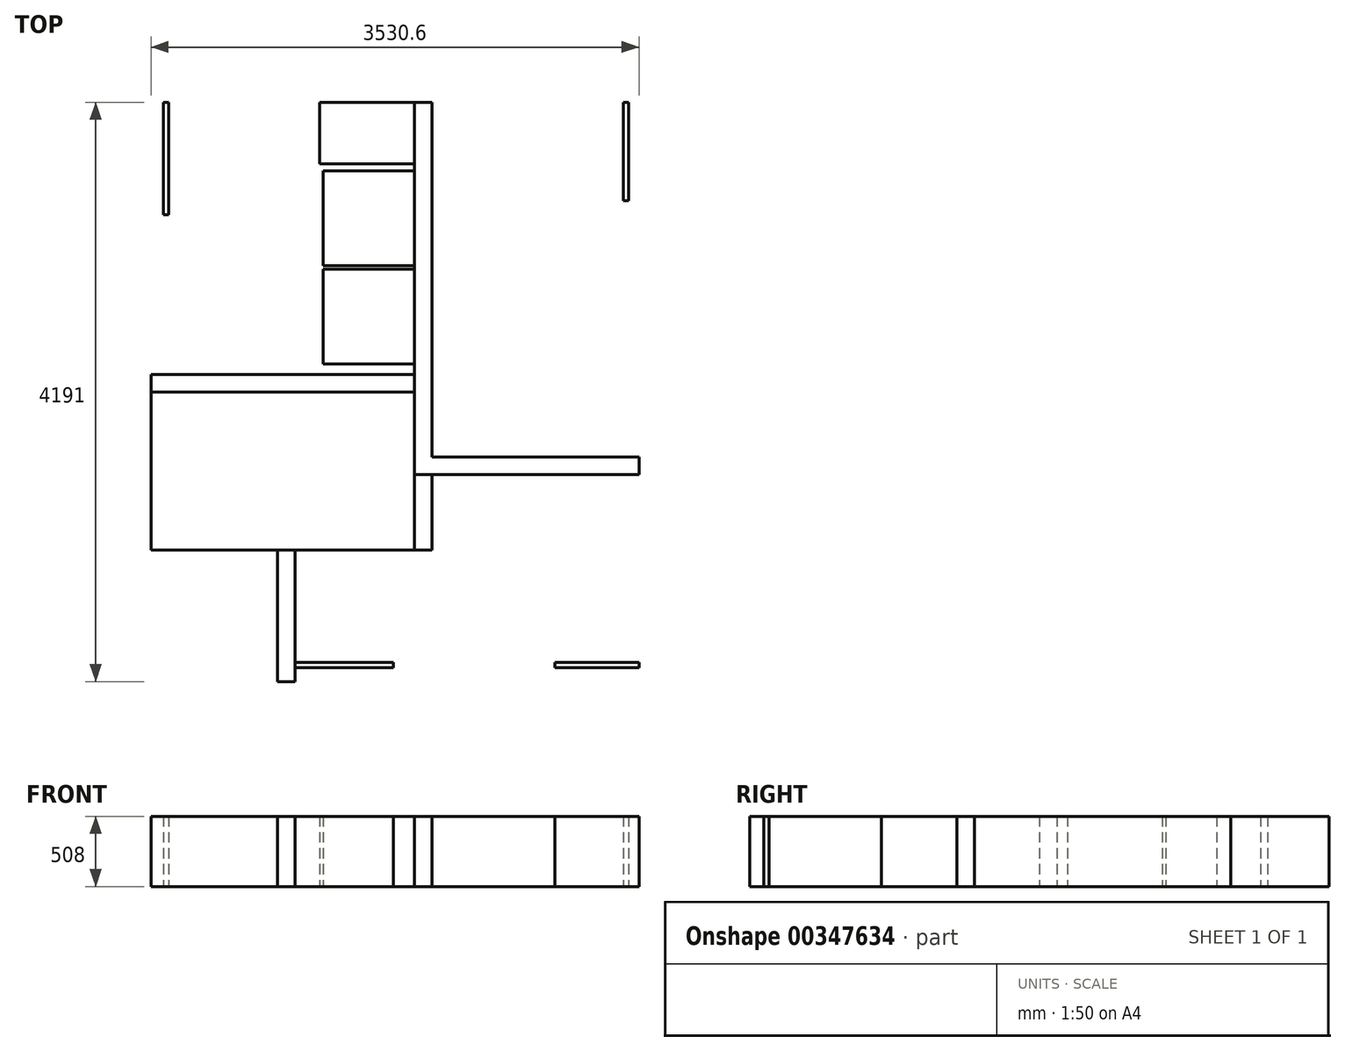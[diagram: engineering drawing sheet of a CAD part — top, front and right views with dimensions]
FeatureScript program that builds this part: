
annotation { "Feature Type Name" : "Feature", "Feature Type Description" : "" }
export const myFeature = defineFeature(function(context is Context, id is Id, definition is map)
    precondition{}
    {
        {
            var Q0;
            Q0=qCreatedBy(makeId("Top.planeOp"),FACE);
            var sketch = newSketch(context, id + "F0", { "sketchPlane" : qUnion([Q0])});
            skLineSegment(sketch, "E0.bottom", {"start": v(-1784.47, 1899.05) * mm, "end": v(1746.13, 1899.05) * mm, "construction": true});
            skLineSegment(sketch, "E0.top", {"start": v(-1784.47, -2291.95) * mm, "end": v(1746.13, -2291.95) * mm, "construction": true});
            skLineSegment(sketch, "E0.left", {"start": v(-1784.47, 1899.05) * mm, "end": v(-1784.47, -2291.95) * mm, "construction": true});
            skLineSegment(sketch, "E0.right", {"start": v(1746.13, 1899.05) * mm, "end": v(1746.13, -2291.95) * mm, "construction": true});
            skLineSegment(sketch, "E1.bottom", {"start": v(-1784.47, 1899.05) * mm, "end": v(1746.13, 1899.05) * mm});
            skLineSegment(sketch, "E1.top", {"start": v(-1784.47, -2291.95) * mm, "end": v(1746.13, -2291.95) * mm});
            skLineSegment(sketch, "E1.left", {"start": v(-1784.47, 1899.05) * mm, "end": v(-1784.47, -2291.95) * mm});
            skLineSegment(sketch, "E1.right", {"start": v(1746.13, 1899.05) * mm, "end": v(1746.13, -2291.95) * mm});
            skSolve(sketch);
        }
        {
            var Q0;
            Q0=qCreatedBy(makeId("Top.planeOp"),FACE);
            var sketch = newSketch(context, id + "F1", { "sketchPlane" : qUnion([Q0])});
            skLineSegment(sketch, "E2.bottom", {"start": v(-565.27, 1899.05) * mm, "end": v(120.53, 1899.05) * mm});
            skLineSegment(sketch, "E2.top", {"start": v(-565.27, 1454.55) * mm, "end": v(120.53, 1454.55) * mm});
            skLineSegment(sketch, "E2.left", {"start": v(-565.27, 1899.05) * mm, "end": v(-565.27, 1454.55) * mm});
            skLineSegment(sketch, "E2.right", {"start": v(120.53, 1899.05) * mm, "end": v(120.53, 1454.55) * mm});
            skSolve(sketch);
        }
        {
            var Q0;
            Q0=qCreatedBy(makeId("Top.planeOp"),FACE);
            var sketch = newSketch(context, id + "F2", { "sketchPlane" : qUnion([Q0])});
            skLineSegment(sketch, "E3.bottom", {"start": v(1746.13, -793.35) * mm, "end": v(120.53, -793.35) * mm});
            skLineSegment(sketch, "E3.top", {"start": v(1746.13, -666.35) * mm, "end": v(120.53, -666.35) * mm});
            skLineSegment(sketch, "E3.left", {"start": v(1746.13, -793.35) * mm, "end": v(1746.13, -666.35) * mm});
            skLineSegment(sketch, "E3.right", {"start": v(120.53, -793.35) * mm, "end": v(120.53, -666.35) * mm});
            skLineSegment(sketch, "E4.bottom", {"start": v(120.53, -666.35) * mm, "end": v(247.53, -666.35) * mm});
            skLineSegment(sketch, "E4.top", {"start": v(120.53, 1899.05) * mm, "end": v(247.53, 1899.05) * mm});
            skLineSegment(sketch, "E4.left", {"start": v(120.53, -666.35) * mm, "end": v(120.53, 1899.05) * mm});
            skLineSegment(sketch, "E4.right", {"start": v(247.53, -666.35) * mm, "end": v(247.53, 1899.05) * mm});
            skLineSegment(sketch, "E5.bottom", {"start": v(120.53, -793.35) * mm, "end": v(247.53, -793.35) * mm});
            skSolve(sketch);
        }
        {
            var Q0;
            Q0=qCreatedBy(makeId("Top.planeOp"),FACE);
            var sketch = newSketch(context, id + "F3", { "sketchPlane" : qUnion([Q0])});
            skLineSegment(sketch, "E6.bottom", {"start": v(1136.53, -2152.25) * mm, "end": v(1746.13, -2152.25) * mm});
            skLineSegment(sketch, "E6.top", {"start": v(1136.53, -2190.35) * mm, "end": v(1746.13, -2190.35) * mm});
            skLineSegment(sketch, "E6.left", {"start": v(1136.53, -2190.35) * mm, "end": v(1136.53, -2152.25) * mm});
            skLineSegment(sketch, "E6.right", {"start": v(1746.13, -2190.35) * mm, "end": v(1746.13, -2152.25) * mm});
            skArc(sketch, "E7", {"start": v(1136.53, -2190.35) * mm, "mid": v(1315.08, -1759.3) * mm, "end": v(1746.13, -1580.75) * mm});
            skSolve(sketch);
        }
        {
            var Q0;
            Q0=qCreatedBy(makeId("Top.planeOp"),FACE);
            var sketch = newSketch(context, id + "F4", { "sketchPlane" : qUnion([Q0])});
            skLineSegment(sketch, "E8.bottom", {"start": v(-539.87, 6.75) * mm, "end": v(-539.87, 692.55) * mm});
            skLineSegment(sketch, "E8.top", {"start": v(120.53, 6.75) * mm, "end": v(120.53, 692.55) * mm});
            skLineSegment(sketch, "E8.left", {"start": v(-539.87, 6.75) * mm, "end": v(120.53, 6.75) * mm});
            skLineSegment(sketch, "E8.right", {"start": v(-539.87, 692.55) * mm, "end": v(120.53, 692.55) * mm});
            skLineSegment(sketch, "E9.bottom", {"start": v(-539.87, 717.95) * mm, "end": v(-539.87, 1403.75) * mm});
            skLineSegment(sketch, "E9.top", {"start": v(120.53, 717.95) * mm, "end": v(120.53, 1403.75) * mm});
            skLineSegment(sketch, "E9.left", {"start": v(-539.87, 717.95) * mm, "end": v(120.53, 717.95) * mm});
            skLineSegment(sketch, "E9.right", {"start": v(-539.87, 1403.75) * mm, "end": v(120.53, 1403.75) * mm});
            skSolve(sketch);
        }
        {
            var Q0;
            Q0=qCreatedBy(makeId("Top.planeOp"),FACE);
            var sketch = newSketch(context, id + "F5", { "sketchPlane" : qUnion([Q0])});
            skLineSegment(sketch, "E10.bottom", {"start": v(1669.93, 1899.05) * mm, "end": v(1631.83, 1899.05) * mm});
            skLineSegment(sketch, "E10.top", {"start": v(1669.93, 1187.85) * mm, "end": v(1631.83, 1187.85) * mm});
            skLineSegment(sketch, "E10.left", {"start": v(1669.93, 1899.05) * mm, "end": v(1669.93, 1187.85) * mm});
            skLineSegment(sketch, "E10.right", {"start": v(1631.83, 1899.05) * mm, "end": v(1631.83, 1187.85) * mm});
            skArc(sketch, "E11", {"start": v(1669.93, 1187.85) * mm, "mid": v(1167.04, 1396.16) * mm, "end": v(958.73, 1899.05) * mm});
            skSolve(sketch);
        }
        {
            var Q0;
            Q0=qCreatedBy(makeId("Top.planeOp"),FACE);
            var sketch = newSketch(context, id + "F6", { "sketchPlane" : qUnion([Q0])});
            skLineSegment(sketch, "E12.bottom", {"start": v(-1695.57, 1899.05) * mm, "end": v(-1657.47, 1899.05) * mm});
            skLineSegment(sketch, "E12.top", {"start": v(-1695.57, 1086.25) * mm, "end": v(-1657.47, 1086.25) * mm});
            skLineSegment(sketch, "E12.left", {"start": v(-1695.57, 1899.05) * mm, "end": v(-1695.57, 1086.25) * mm});
            skLineSegment(sketch, "E12.right", {"start": v(-1657.47, 1899.05) * mm, "end": v(-1657.47, 1086.25) * mm});
            skArc(sketch, "E13", {"start": v(-1695.57, 1086.25) * mm, "mid": v(-1120.83, 1324.31) * mm, "end": v(-882.77, 1899.05) * mm});
            skSolve(sketch);
        }
        {
            var Q0;
            Q0=qCreatedBy(makeId("Top.planeOp"),FACE);
            var sketch = newSketch(context, id + "F7", { "sketchPlane" : qUnion([Q0])});
            skLineSegment(sketch, "E14.bottom", {"start": v(-743.07, -1339.45) * mm, "end": v(-870.07, -1339.45) * mm});
            skLineSegment(sketch, "E14.top", {"start": v(-743.07, -2291.95) * mm, "end": v(-870.07, -2291.95) * mm});
            skLineSegment(sketch, "E14.left", {"start": v(-743.07, -1339.45) * mm, "end": v(-743.07, -2291.95) * mm});
            skLineSegment(sketch, "E14.right", {"start": v(-870.07, -1339.45) * mm, "end": v(-870.07, -2291.95) * mm});
            skSolve(sketch);
        }
        {
            var Q0;
            Q0=qCreatedBy(makeId("Top.planeOp"),FACE);
            var sketch = newSketch(context, id + "F8", { "sketchPlane" : qUnion([Q0])});
            skLineSegment(sketch, "E15.left", {"start": v(120.53, -69.45) * mm, "end": v(120.53, -196.45) * mm});
            skLineSegment(sketch, "E16.left", {"start": v(-1784.47, -69.45) * mm, "end": v(-1784.47, -196.45) * mm});
            skLineSegment(sketch, "E17", {"start": v(-1784.47, -196.45) * mm, "end": v(120.53, -196.45) * mm});
            skLineSegment(sketch, "E18", {"start": v(-1784.47, -69.45) * mm, "end": v(120.53, -69.45) * mm});
            skSolve(sketch);
        }
        {
            var Q0;
            Q0=makeQuery(id+"F0.imprint","IMPRINT",FACE,{"disambiguationData":[TD([[makeQuery(id+"F0.imprint","IMPRINT",EDGE,{"derivedFrom":sQuery(id+"F0.wireOp",EDGE,"E1.bottom")}),-1.0]])]});
            var sketch = newSketch(context, id + "F9", { "sketchPlane" : qUnion([Q0])});
            skLineSegment(sketch, "E19.bottom", {"start": v(120.53, -196.45) * mm, "end": v(-1784.47, -196.45) * mm});
            skLineSegment(sketch, "E19.top", {"start": v(120.53, -1339.45) * mm, "end": v(-1784.47, -1339.45) * mm});
            skLineSegment(sketch, "E19.left", {"start": v(120.53, -196.45) * mm, "end": v(120.53, -1339.45) * mm});
            skLineSegment(sketch, "E19.right", {"start": v(-1784.47, -196.45) * mm, "end": v(-1784.47, -1339.45) * mm});
            skSolve(sketch);
        }
        {
            var Q0;
            Q0=makeQuery(id+"F0.imprint","IMPRINT",FACE,{"disambiguationData":[TD([[makeQuery(id+"F0.imprint","IMPRINT",EDGE,{"derivedFrom":sQuery(id+"F0.wireOp",EDGE,"E1.bottom")}),-1.0]])]});
            var sketch = newSketch(context, id + "F10", { "sketchPlane" : qUnion([Q0])});
            skLineSegment(sketch, "E20.bottom", {"start": v(247.53, -793.35) * mm, "end": v(120.53, -793.35) * mm});
            skLineSegment(sketch, "E20.top", {"start": v(247.53, -1339.45) * mm, "end": v(120.53, -1339.45) * mm});
            skLineSegment(sketch, "E20.left", {"start": v(247.53, -793.35) * mm, "end": v(247.53, -1339.45) * mm});
            skLineSegment(sketch, "E20.right", {"start": v(120.53, -793.35) * mm, "end": v(120.53, -1339.45) * mm});
            skSolve(sketch);
        }
        {
            var Q0;
            Q0=makeQuery(id+"F0.imprint","IMPRINT",FACE,{"disambiguationData":[TD([[makeQuery(id+"F0.imprint","IMPRINT",EDGE,{"derivedFrom":sQuery(id+"F0.wireOp",EDGE,"E1.bottom")}),-1.0]])]});
            var sketch = newSketch(context, id + "F11", { "sketchPlane" : qUnion([Q0])});
            skLineSegment(sketch, "E21.bottom", {"start": v(-743.07, -2190.35) * mm, "end": v(-31.87, -2190.35) * mm});
            skLineSegment(sketch, "E21.top", {"start": v(-743.07, -2152.25) * mm, "end": v(-31.87, -2152.25) * mm});
            skLineSegment(sketch, "E21.left", {"start": v(-743.07, -2190.35) * mm, "end": v(-743.07, -2152.25) * mm});
            skLineSegment(sketch, "E21.right", {"start": v(-31.87, -2190.35) * mm, "end": v(-31.87, -2152.25) * mm});
            skArc(sketch, "E22", {"start": v(-31.87, -2190.35) * mm, "mid": v(-240.17, -1687.46) * mm, "end": v(-743.07, -1479.15) * mm});
            skSolve(sketch);
        }
        {
            var Q0;
            Q0 = qSketchRegion(id + "F9", true);
            var Q1;
            Q1 = qSketchRegion(id + "F8", true);
            var Q2;
            Q2 = qSketchRegion(id + "F7", true);
            var Q3;
            Q3 = qSketchRegion(id + "F6", true);
            var Q4;
            Q4 = qSketchRegion(id + "F5", true);
            var Q5;
            Q5 = qSketchRegion(id + "F4", true);
            var Q6;
            Q6 = qSketchRegion(id + "F3", true);
            var Q7;
            Q7 = qSketchRegion(id + "F1", true);
            var Q8;
            Q8 = qSketchRegion(id + "F10", true);
            var Q9;
            Q9 = qSketchRegion(id + "F11", true);
            extrude(context, id + "F12", {"entities" : qUnion([Q0, Q1, Q2, Q3, Q4, Q5, Q6, Q7, Q8, Q9]), "depth" : 508 * mm, "offsetDistance" : 25.4 * mm});
        }
        {
            var Q0;
            Q0=makeQuery(id+"F2.imprint","IMPRINT",FACE,{"disambiguationData":[TD([[makeQuery(id+"F2.imprint","IMPRINT",EDGE,{"derivedFrom":sQuery(id+"F2.wireOp",EDGE,"E4.bottom")}),1.0]])]});
            var Q1;
            Q1 = qSketchRegion(id + "F2", true);
            extrude(context, id + "F13", {"entities" : qUnion([Q0, Q1]), "depth" : 508 * mm, "offsetDistance" : 25.4 * mm});
        }
        {
            var Q0;
            Q0=sQuery(id+"F3.wireOp",EDGE,"E7");
            var Q1;
            Q1=sQuery(id+"F6.wireOp",EDGE,"E13");
            var Q2;
            Q2=sQuery(id+"F5.wireOp",EDGE,"E11");
            var Q3;
            Q3=sQuery(id+"F11.wireOp",EDGE,"E22");
            extrude(context, id + "F14", {"bodyType" : ToolBodyType.SURFACE, "surfaceEntities" : qUnion([Q0, Q1, Q2, Q3]), "depth" : 508 * mm, "offsetDistance" : 25.4 * mm});
        }
    });
